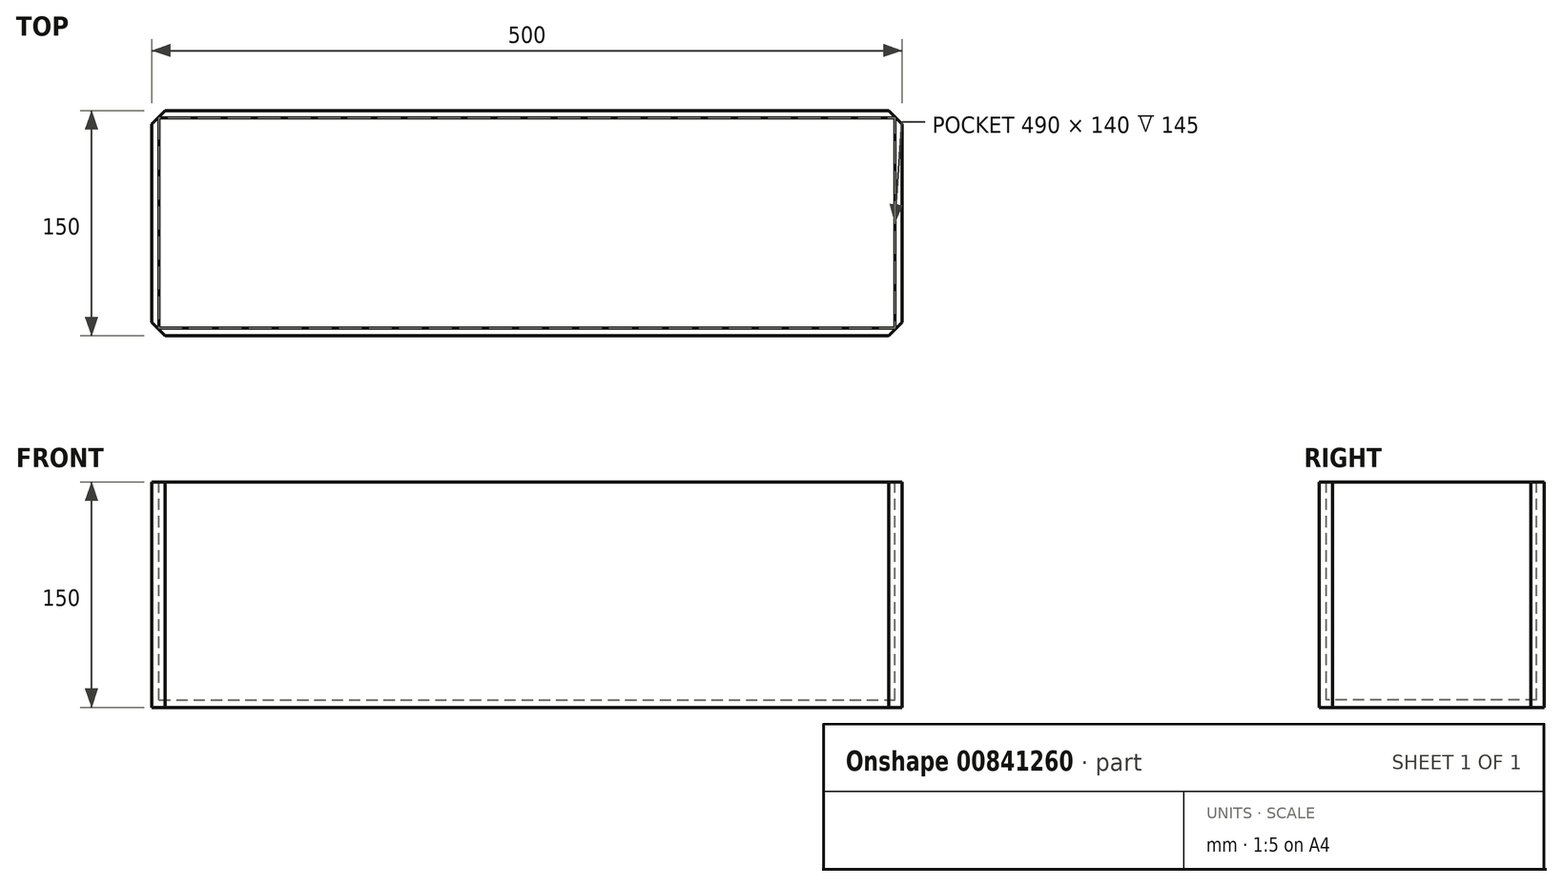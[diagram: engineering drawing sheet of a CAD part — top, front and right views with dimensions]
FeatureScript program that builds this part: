
annotation { "Feature Type Name" : "Feature", "Feature Type Description" : "" }
export const myFeature = defineFeature(function(context is Context, id is Id, definition is map)
    precondition{}
    {
        {
            var Q0;
            Q0=qCreatedBy(makeId("Top.planeOp"),FACE);
            var sketch = newSketch(context, id + "F0", { "sketchPlane" : qUnion([Q0])});
            skLineSegment(sketch, "E0.bottom", {"start": v(-246.14, 77.15) * mm, "end": v(253.86, 77.15) * mm});
            skLineSegment(sketch, "E0.top", {"start": v(-246.14, -72.85) * mm, "end": v(253.86, -72.85) * mm});
            skLineSegment(sketch, "E0.left", {"start": v(-246.14, 77.15) * mm, "end": v(-246.14, -72.85) * mm});
            skLineSegment(sketch, "E0.right", {"start": v(253.86, 77.15) * mm, "end": v(253.86, -72.85) * mm});
            skSolve(sketch);
        }
        {
            var Q0;
            Q0 = qSketchRegion(id + "F0", true);
            extrude(context, id + "F1", {"entities" : qUnion([Q0]), "depth" : 150 * mm, "offsetDistance" : 25 * mm});
        }
        {
            var Q0;
            Q0=makeQuery(id+"F1.opExtrude","CAP_FACE",FACE,{"disambiguationData":[OSD([sQuery(id+"F0.wireOp",EDGE,"E0.bottom"),sQuery(id+"F0.wireOp",EDGE,"E0.top"),sQuery(id+"F0.wireOp",EDGE,"E0.left"),sQuery(id+"F0.wireOp",EDGE,"E0.right")])],"isStart":false});
            var sketch = newSketch(context, id + "F2", { "sketchPlane" : qUnion([Q0])});
            skLineSegment(sketch, "E1.bottom", {"start": v(-241.14, 72.15) * mm, "end": v(248.86, 72.15) * mm});
            skLineSegment(sketch, "E1.top", {"start": v(-241.14, -67.85) * mm, "end": v(248.86, -67.85) * mm});
            skLineSegment(sketch, "E1.left", {"start": v(-241.14, 72.15) * mm, "end": v(-241.14, -67.85) * mm});
            skLineSegment(sketch, "E1.right", {"start": v(248.86, 72.15) * mm, "end": v(248.86, -67.85) * mm});
            skSolve(sketch);
        }
        {
            var Q0;
            Q0 = qSketchRegion(id + "F2", true);
            extrude(context, id + "F3", {"entities" : qUnion([Q0]), "operationType" : NewBodyOperationType.REMOVE, "oppositeDirection" : true, "depth" : 145 * mm, "offsetDistance" : 25 * mm});
        }
        {
            var Q0;
            Q0=makeQuery(id+"F1.opExtrude","SWEPT_EDGE",EDGE,{"disambiguationData":[OSD([sQuery(id+"F0.wireOp",EDGE,"E0.top"),sQuery(id+"F0.wireOp",EDGE,"E0.right")])]});
            chamfer(context, id + "F4", {"entities" : qUnion([Q0]), "width" : 9 * mm, "tangentPropagation" : true});
        }
        {
            var Q0;
            Q0=makeQuery(id+"F1.opExtrude","SWEPT_EDGE",EDGE,{"disambiguationData":[OSD([sQuery(id+"F0.wireOp",EDGE,"E0.bottom"),sQuery(id+"F0.wireOp",EDGE,"E0.right")])]});
            var Q1;
            Q1=makeQuery(id+"F1.opExtrude","SWEPT_EDGE",EDGE,{"disambiguationData":[OSD([sQuery(id+"F0.wireOp",EDGE,"E0.bottom"),sQuery(id+"F0.wireOp",EDGE,"E0.left")])]});
            var Q2;
            Q2=makeQuery(id+"F1.opExtrude","SWEPT_EDGE",EDGE,{"disambiguationData":[OSD([sQuery(id+"F0.wireOp",EDGE,"E0.top"),sQuery(id+"F0.wireOp",EDGE,"E0.left")])]});
            chamfer(context, id + "F5", {"entities" : qUnion([Q0, Q1, Q2]), "width" : 9 * mm, "tangentPropagation" : true});
        }
    });
